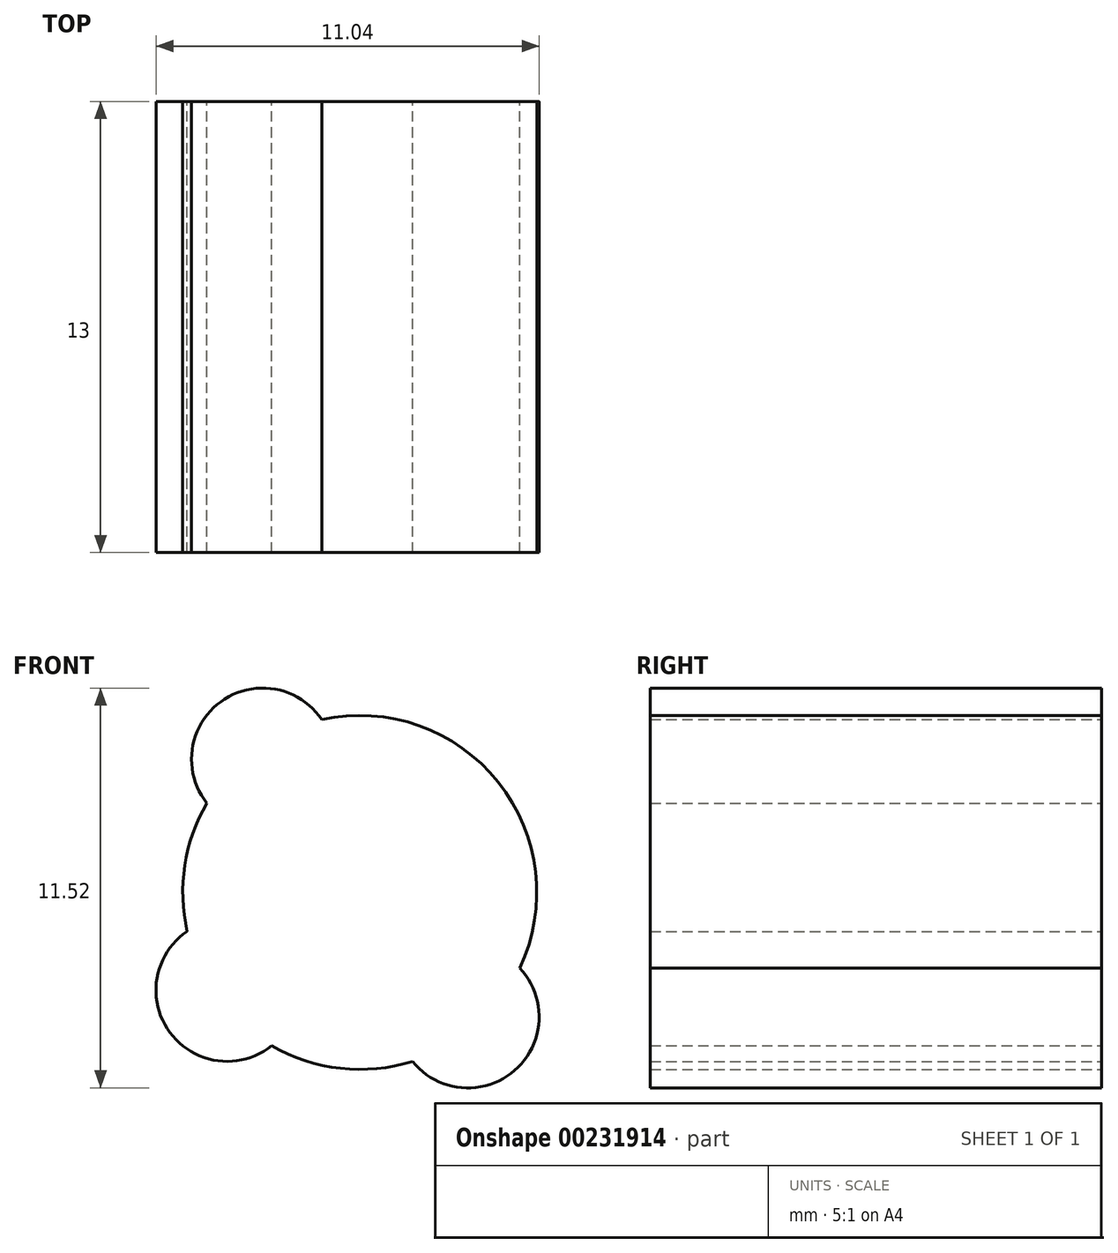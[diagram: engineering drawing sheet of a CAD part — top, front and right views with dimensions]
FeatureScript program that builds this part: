
annotation { "Feature Type Name" : "Feature", "Feature Type Description" : "" }
export const myFeature = defineFeature(function(context is Context, id is Id, definition is map)
    precondition{}
    {
        {
            var Q0;
            Q0=qCreatedBy(makeId("Front.planeOp"),FACE);
            var sketch = newSketch(context, id + "F0", { "sketchPlane" : qUnion([Q0])});
            skArc(sketch, "E0", {"start": v(1.15, 4.97) * mm, "mid": v(0.03, 5.1) * mm, "end": v(-1.1, 4.98) * mm});
            skCircle(sketch, "E1", {"center": v(0, 0) * mm, "radius": 6.8 * mm, "construction": true});
            skArc(sketch, "E2", {"start": v(-1.1, 4.98) * mm, "mid": v(-4, 5.5) * mm, "end": v(-4.4, 2.57) * mm});
            skArc(sketch, "E3", {"start": v(-4.97, -1.12) * mm, "mid": v(-5.47, -4.04) * mm, "end": v(-2.54, -4.42) * mm});
            skArc(sketch, "E4", {"start": v(1.52, -4.87) * mm, "mid": v(4.46, -5.13) * mm, "end": v(4.61, -2.18) * mm});
            skArc(sketch, "E5.trimOffspring", {"start": v(-4.4, 2.57) * mm, "mid": v(-5.04, 0.78) * mm, "end": v(-4.97, -1.12) * mm});
            skArc(sketch, "E6.trimOffspring", {"start": v(-2.54, -4.42) * mm, "mid": v(-0.56, -5.07) * mm, "end": v(1.52, -4.87) * mm});
            skArc(sketch, "E7.trimOffspring", {"start": v(4.61, -2.18) * mm, "mid": v(4.6, 2.22) * mm, "end": v(1.15, 4.97) * mm});
            skSolve(sketch);
        }
        {
            var Q0;
            Q0=makeQuery(id+"F0.imprint","IMPRINT",FACE,{"disambiguationData":[TD([[makeQuery(id+"F0.imprint","IMPRINT",EDGE,{"derivedFrom":sQuery(id+"F0.wireOp",EDGE,"E0")}),1.0]])]});
            extrude(context, id + "F1", {"entities" : qUnion([Q0]), "depth" : 13 * mm});
        }
    });
